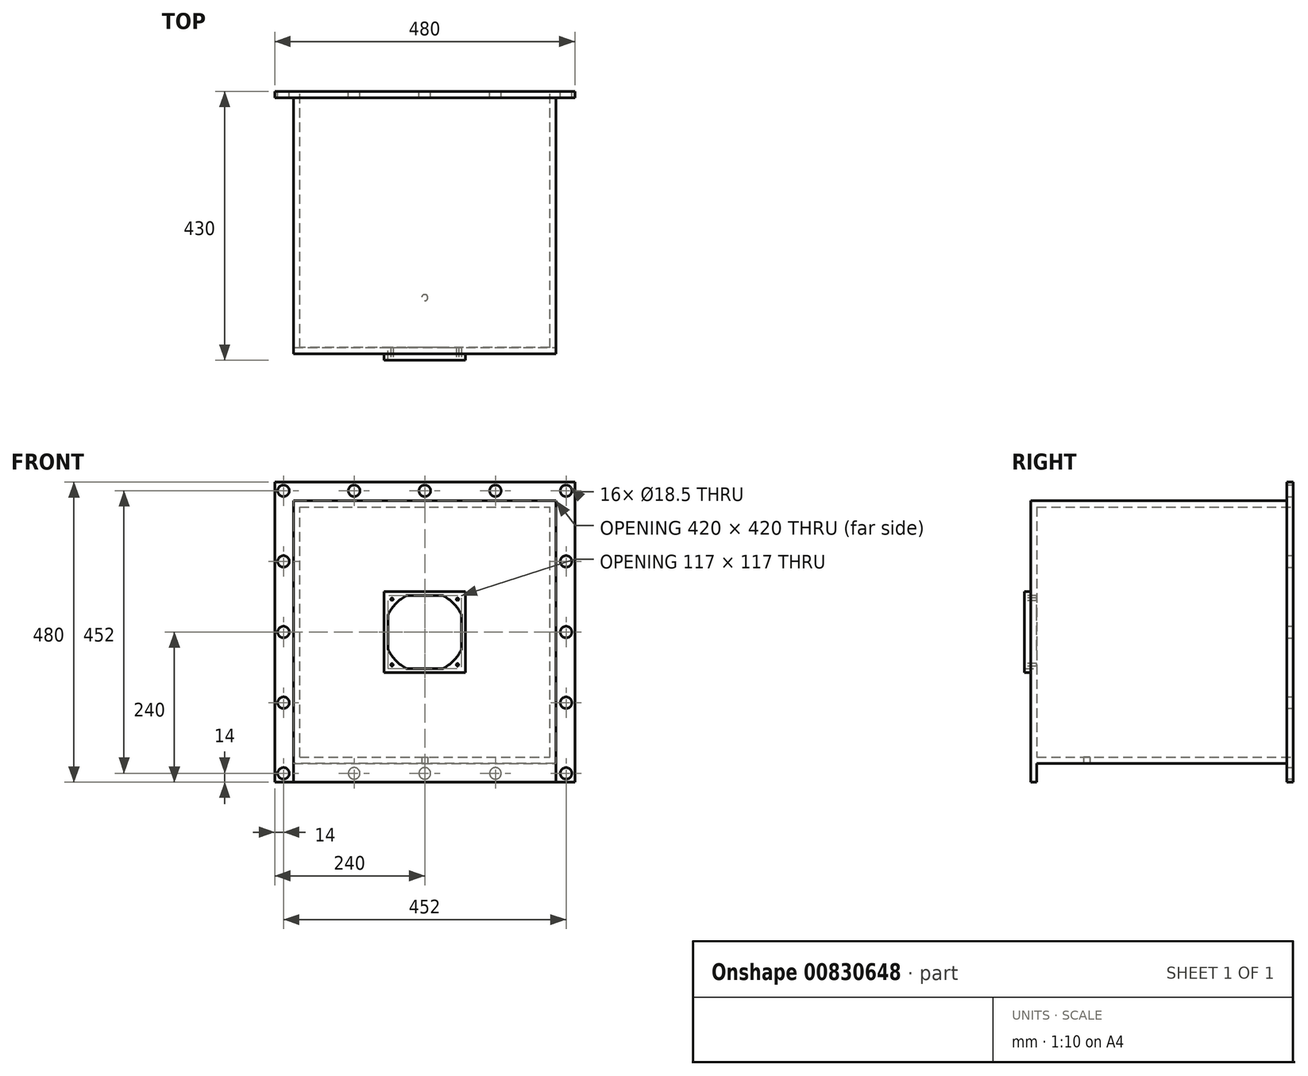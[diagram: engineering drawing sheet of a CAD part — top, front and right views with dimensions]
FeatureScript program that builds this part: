
annotation { "Feature Type Name" : "Feature", "Feature Type Description" : "" }
export const myFeature = defineFeature(function(context is Context, id is Id, definition is map)
    precondition{}
    {
        {
            var Q0;
            Q0=qCreatedBy(makeId("Front.planeOp"),FACE);
            var sketch = newSketch(context, id + "F0", { "sketchPlane" : qUnion([Q0])});
            skLineSegment(sketch, "E0", {"start": v(0, 306.37) * mm, "end": v(0, -317.21) * mm, "construction": true});
            skLineSegment(sketch, "E1", {"start": v(-443.03, 0) * mm, "end": v(583.03, 0) * mm, "construction": true});
            skLineSegment(sketch, "E2.bottom", {"start": v(-210, 210) * mm, "end": v(210, 210) * mm});
            skLineSegment(sketch, "E2.top", {"start": v(-210, -210) * mm, "end": v(210, -210) * mm});
            skLineSegment(sketch, "E2.left", {"start": v(-210, 210) * mm, "end": v(-210, -210) * mm});
            skLineSegment(sketch, "E2.right", {"start": v(210, 210) * mm, "end": v(210, -210) * mm});
            skSolve(sketch);
        }
        {
            var Q0;
            Q0 = qSketchRegion(id + "F0", true);
            extrude(context, id + "F1", {"entities" : qUnion([Q0]), "depth" : 420 * mm, "offsetDistance" : 25 * mm});
        }
        {
            var Q0;
            Q0=makeQuery(id+"F0.imprint","IMPRINT",FACE,{"disambiguationData":[TD([[makeQuery(id+"F0.imprint","IMPRINT",EDGE,{"derivedFrom":sQuery(id+"F0.wireOp",EDGE,"E2.bottom")}),-1.0]])]});
            var sketch = newSketch(context, id + "F2", { "sketchPlane" : qUnion([Q0])});
            skLineSegment(sketch, "E3.bottom", {"start": v(200, 200) * mm, "end": v(-200, 200) * mm});
            skLineSegment(sketch, "E3.top", {"start": v(200, -200) * mm, "end": v(-200, -200) * mm});
            skLineSegment(sketch, "E3.left", {"start": v(200, 200) * mm, "end": v(200, -200) * mm});
            skLineSegment(sketch, "E3.right", {"start": v(-200, 200) * mm, "end": v(-200, -200) * mm});
            skSolve(sketch);
        }
        {
            var Q0;
            Q0 = qSketchRegion(id + "F2", true);
            extrude(context, id + "F3", {"entities" : qUnion([Q0]), "operationType" : NewBodyOperationType.REMOVE, "depth" : 410 * mm, "offsetDistance" : 25 * mm});
        }
        {
            var Q0;
            Q0=makeQuery(id+"F0.imprint","IMPRINT",FACE,{"disambiguationData":[TD([[makeQuery(id+"F0.imprint","IMPRINT",EDGE,{"derivedFrom":sQuery(id+"F0.wireOp",EDGE,"E2.bottom")}),-1.0]])]});
            var sketch = newSketch(context, id + "F4", { "sketchPlane" : qUnion([Q0])});
            skLineSegment(sketch, "E4.0", {"start": v(-240, 240) * mm, "end": v(240, 240) * mm});
            skLineSegment(sketch, "E4.1", {"start": v(-240, 240) * mm, "end": v(-240, -240) * mm});
            skLineSegment(sketch, "E4.2", {"start": v(-240, -240) * mm, "end": v(240, -240) * mm});
            skLineSegment(sketch, "E4.3", {"start": v(240, 240) * mm, "end": v(240, -240) * mm});
            skLineSegment(sketch, "E5.0", {"start": v(210, 210) * mm, "end": v(210, -210) * mm});
            skLineSegment(sketch, "E6.0", {"start": v(-210, 210) * mm, "end": v(210, 210) * mm});
            skLineSegment(sketch, "E7.0", {"start": v(-210, 210) * mm, "end": v(-210, -210) * mm});
            skLineSegment(sketch, "E8.0", {"start": v(-210, -210) * mm, "end": v(210, -210) * mm});
            skSolve(sketch);
        }
        {
            var Q0;
            Q0 = qSketchRegion(id + "F4", true);
            extrude(context, id + "F5", {"entities" : qUnion([Q0]), "operationType" : NewBodyOperationType.ADD, "depth" : 10 * mm, "offsetDistance" : 25 * mm});
        }
        {
            var Q0;
            Q0=makeQuery(id+"F1.opExtrude","CAP_FACE",FACE,{"disambiguationData":[OSD([sQuery(id+"F0.wireOp",EDGE,"E2.bottom"),sQuery(id+"F0.wireOp",EDGE,"E2.top"),sQuery(id+"F0.wireOp",EDGE,"E2.left"),sQuery(id+"F0.wireOp",EDGE,"E2.right")])],"isStart":false});
            var sketch = newSketch(context, id + "F6", { "sketchPlane" : qUnion([Q0])});
            skLineSegment(sketch, "E9", {"start": v(0, 340.6) * mm, "end": v(0, -378.07) * mm, "construction": true});
            skPoint(sketch, "E9.endSnap0", {"position": v(0, -210) * mm});
            skLineSegment(sketch, "E10", {"start": v(-383.48, 0) * mm, "end": v(426.16, 0) * mm, "construction": true});
            skLineSegment(sketch, "E11.bottom", {"start": v(-65, 65) * mm, "end": v(65, 65) * mm});
            skLineSegment(sketch, "E11.top", {"start": v(-65, -65) * mm, "end": v(65, -65) * mm});
            skLineSegment(sketch, "E11.left", {"start": v(-65, 65) * mm, "end": v(-65, -65) * mm});
            skLineSegment(sketch, "E11.right", {"start": v(65, 65) * mm, "end": v(65, -65) * mm});
            skSolve(sketch);
        }
        {
            var Q0;
            Q0 = qSketchRegion(id + "F6", true);
            extrude(context, id + "F7", {"entities" : qUnion([Q0]), "operationType" : NewBodyOperationType.ADD, "depth" : 10 * mm, "offsetDistance" : 25 * mm});
        }
        {
            var Q0;
            Q0=makeQuery(id+"F7.opExtrude","CAP_FACE",FACE,{"disambiguationData":[OSD([sQuery(id+"F6.wireOp",EDGE,"E11.bottom"),sQuery(id+"F6.wireOp",EDGE,"E11.top"),sQuery(id+"F6.wireOp",EDGE,"E11.left"),sQuery(id+"F6.wireOp",EDGE,"E11.right")])],"isStart":false});
            var sketch = newSketch(context, id + "F8", { "sketchPlane" : qUnion([Q0])});
            skLineSegment(sketch, "E12", {"start": v(0, 129.06) * mm, "end": v(0, -141.19) * mm, "construction": true});
            skLineSegment(sketch, "E13", {"start": v(-149.42, 0) * mm, "end": v(152.02, 0) * mm, "construction": true});
            skArc(sketch, "E14", {"start": v(-28.33, 58.5) * mm, "mid": v(-45.96, 45.96) * mm, "end": v(-58.5, 28.33) * mm});
            skLineSegment(sketch, "E15.bottom", {"start": v(-28.33, 58.5) * mm, "end": v(28.33, 58.5) * mm});
            skLineSegment(sketch, "E15.top", {"start": v(-28.33, -58.5) * mm, "end": v(28.33, -58.5) * mm});
            skLineSegment(sketch, "E15.left", {"start": v(-58.5, 28.33) * mm, "end": v(-58.5, -28.33) * mm});
            skLineSegment(sketch, "E15.right", {"start": v(58.5, 28.33) * mm, "end": v(58.5, -28.33) * mm});
            skArc(sketch, "E16.trimOffspring", {"start": v(-58.5, -28.33) * mm, "mid": v(-45.96, -45.96) * mm, "end": v(-28.33, -58.5) * mm});
            skArc(sketch, "E17.trimOffspring", {"start": v(28.33, -58.5) * mm, "mid": v(45.96, -45.96) * mm, "end": v(58.5, -28.33) * mm});
            skArc(sketch, "E18.trimOffspring", {"start": v(58.5, 28.33) * mm, "mid": v(45.96, 45.96) * mm, "end": v(28.33, 58.5) * mm});
            skSolve(sketch);
        }
        {
            var Q0;
            Q0 = qSketchRegion(id + "F8", true);
            extrude(context, id + "F9", {"entities" : qUnion([Q0]), "operationType" : NewBodyOperationType.REMOVE, "endBound" : BoundingType.UP_TO_NEXT, "oppositeDirection" : true, "depth" : 25 * mm, "offsetDistance" : 25 * mm});
        }
        {
            var Q0;
            Q0=makeQuery(id+"F7.opExtrude","CAP_FACE",FACE,{"disambiguationData":[OSD([sQuery(id+"F6.wireOp",EDGE,"E11.bottom"),sQuery(id+"F6.wireOp",EDGE,"E11.top"),sQuery(id+"F6.wireOp",EDGE,"E11.left"),sQuery(id+"F6.wireOp",EDGE,"E11.right")])],"isStart":false});
            var sketch = newSketch(context, id + "F10", { "sketchPlane" : qUnion([Q0])});
            skLineSegment(sketch, "E19", {"start": v(0, 121.68) * mm, "end": v(0, -124.9) * mm, "construction": true});
            skLineSegment(sketch, "E20", {"start": v(-130.66, 0) * mm, "end": v(137.37, 0) * mm, "construction": true});
            skCircle(sketch, "E21", {"center": v(52.4, 52.4) * mm, "radius": 2 * mm});
            skCircle(sketch, "E22.MirrorC", {"center": v(52.4, -52.4) * mm, "radius": 2 * mm});
            skCircle(sketch, "E23.MirrorC", {"center": v(-52.4, 52.4) * mm, "radius": 2 * mm});
            skCircle(sketch, "E24.MirrorC", {"center": v(-52.4, -52.4) * mm, "radius": 2 * mm});
            skSolve(sketch);
        }
        {
            var Q0;
            Q0 = qSketchRegion(id + "F10", true);
            extrude(context, id + "F11", {"entities" : qUnion([Q0]), "operationType" : NewBodyOperationType.REMOVE, "endBound" : BoundingType.UP_TO_NEXT, "oppositeDirection" : true, "depth" : 25 * mm, "offsetDistance" : 25 * mm});
        }
        {
            var Q0;
            Q0=makeQuery(id+"F5.boolean.opBoolean","MERGE",FACE,{"derivedFrom":[makeQuery(id+"F1.opExtrude","CAP_FACE",FACE,{"disambiguationData":[OSD([sQuery(id+"F0.wireOp",EDGE,"E2.bottom"),sQuery(id+"F0.wireOp",EDGE,"E2.top"),sQuery(id+"F0.wireOp",EDGE,"E2.left"),sQuery(id+"F0.wireOp",EDGE,"E2.right")])],"isStart":true}),makeQuery(id+"F5.opExtrude","CAP_FACE",FACE,{"disambiguationData":[OSD([sQuery(id+"F4.wireOp",EDGE,"E4.0"),sQuery(id+"F4.wireOp",EDGE,"E4.1"),sQuery(id+"F4.wireOp",EDGE,"E4.2"),sQuery(id+"F4.wireOp",EDGE,"E4.3"),sQuery(id+"F4.wireOp",EDGE,"E5.0"),sQuery(id+"F4.wireOp",EDGE,"E6.0"),sQuery(id+"F4.wireOp",EDGE,"E7.0"),sQuery(id+"F4.wireOp",EDGE,"E8.0")])],"isStart":true})]});
            var sketch = newSketch(context, id + "F12", { "sketchPlane" : qUnion([Q0])});
            skLineSegment(sketch, "E25.0", {"start": v(-210, 210) * mm, "end": v(210, 210) * mm});
            skLineSegment(sketch, "E25.1", {"start": v(-210, 210) * mm, "end": v(-210, -210) * mm});
            skLineSegment(sketch, "E25.2", {"start": v(-210, -210) * mm, "end": v(210, -210) * mm});
            skLineSegment(sketch, "E25.3", {"start": v(210, 210) * mm, "end": v(210, -210) * mm});
            skSolve(sketch);
        }
        {
            var Q0;
            Q0 = qSketchRegion(id + "F12", true);
            extrude(context, id + "F13", {"entities" : qUnion([Q0]), "operationType" : NewBodyOperationType.REMOVE, "oppositeDirection" : true, "depth" : 0.5 * mm, "offsetDistance" : 25 * mm});
        }
        {
            var Q0;
            Q0=makeQuery(id+"F13.boolean.opBoolean","COPY",EDGE,{"derivedFrom":makeQuery(id+"F13.opExtrude","SWEPT_EDGE",EDGE,{"disambiguationData":[OSD([sQuery(id+"F12.wireOp",EDGE,"E25.0"),sQuery(id+"F12.wireOp",EDGE,"E25.1")])]})});
            var Q1;
            Q1=makeQuery(id+"F13.boolean.opBoolean","COPY",EDGE,{"derivedFrom":makeQuery(id+"F13.opExtrude","SWEPT_EDGE",EDGE,{"disambiguationData":[OSD([sQuery(id+"F12.wireOp",EDGE,"E25.0"),sQuery(id+"F12.wireOp",EDGE,"E25.3")])]})});
            var Q2;
            Q2=makeQuery(id+"F13.boolean.opBoolean","COPY",EDGE,{"derivedFrom":makeQuery(id+"F13.opExtrude","SWEPT_EDGE",EDGE,{"disambiguationData":[OSD([sQuery(id+"F12.wireOp",EDGE,"E25.2"),sQuery(id+"F12.wireOp",EDGE,"E25.3")])]})});
            var Q3;
            Q3=makeQuery(id+"F13.boolean.opBoolean","COPY",EDGE,{"derivedFrom":makeQuery(id+"F13.opExtrude","SWEPT_EDGE",EDGE,{"disambiguationData":[OSD([sQuery(id+"F12.wireOp",EDGE,"E25.1"),sQuery(id+"F12.wireOp",EDGE,"E25.2")])]})});
            fillet(context, id + "F14", {"entities" : qUnion([Q0, Q1, Q2, Q3]), "radius" : 2 * mm, "tangentPropagation" : true, "allowEdgeOverflow" : false});
        }
        {
            var Q0;
            Q0=makeQuery(id+"F5.boolean.opBoolean","MERGE",FACE,{"derivedFrom":[makeQuery(id+"F1.opExtrude","CAP_FACE",FACE,{"disambiguationData":[OSD([sQuery(id+"F0.wireOp",EDGE,"E2.bottom"),sQuery(id+"F0.wireOp",EDGE,"E2.top"),sQuery(id+"F0.wireOp",EDGE,"E2.left"),sQuery(id+"F0.wireOp",EDGE,"E2.right")])],"isStart":true}),makeQuery(id+"F5.opExtrude","CAP_FACE",FACE,{"disambiguationData":[OSD([sQuery(id+"F4.wireOp",EDGE,"E4.0"),sQuery(id+"F4.wireOp",EDGE,"E4.1"),sQuery(id+"F4.wireOp",EDGE,"E4.2"),sQuery(id+"F4.wireOp",EDGE,"E4.3"),sQuery(id+"F4.wireOp",EDGE,"E5.0"),sQuery(id+"F4.wireOp",EDGE,"E6.0"),sQuery(id+"F4.wireOp",EDGE,"E7.0"),sQuery(id+"F4.wireOp",EDGE,"E8.0")])],"isStart":true})]});
            var sketch = newSketch(context, id + "F15", { "sketchPlane" : qUnion([Q0])});
            skLineSegment(sketch, "E26.0", {"start": v(226, 226) * mm, "end": v(-226, 226) * mm, "construction": true});
            skLineSegment(sketch, "E26.1", {"start": v(226, 226) * mm, "end": v(226, -226) * mm, "construction": true});
            skLineSegment(sketch, "E26.2", {"start": v(226, -226) * mm, "end": v(-226, -226) * mm, "construction": true});
            skLineSegment(sketch, "E26.3", {"start": v(-226, 226) * mm, "end": v(-226, -226) * mm, "construction": true});
            skCircle(sketch, "E27", {"center": v(-226, 226) * mm, "radius": 9.25 * mm});
            skCircle(sketch, "E28", {"center": v(226, 226) * mm, "radius": 9.25 * mm});
            skCircle(sketch, "E29", {"center": v(-226, -226) * mm, "radius": 9.25 * mm});
            skCircle(sketch, "E30", {"center": v(226, -226) * mm, "radius": 9.25 * mm});
            skCircle(sketch, "E31.1.0.0", {"center": v(-113, 226) * mm, "radius": 9.25 * mm});
            skCircle(sketch, "E31.2.0.0", {"center": v(0, 226) * mm, "radius": 9.25 * mm});
            skCircle(sketch, "E31.3.0.0", {"center": v(113, 226) * mm, "radius": 9.25 * mm});
            skLineSegment(sketch, "E31.direction1", {"start": v(-226, 226) * mm, "end": v(-113, 226) * mm, "construction": true});
            skLineSegment(sketch, "E32", {"start": v(0, 329.24) * mm, "end": v(0, -280.21) * mm, "construction": true});
            skLineSegment(sketch, "E33", {"start": v(-290.82, 0) * mm, "end": v(280.62, 0) * mm, "construction": true});
            skCircle(sketch, "E34.0.1.0", {"center": v(-226, -113) * mm, "radius": 9.25 * mm});
            skCircle(sketch, "E34.0.2.0", {"center": v(-226, 0) * mm, "radius": 9.25 * mm});
            skCircle(sketch, "E34.0.3.0", {"center": v(-226, 113) * mm, "radius": 9.25 * mm});
            skLineSegment(sketch, "E34.direction1", {"start": v(-226, -226) * mm, "end": v(-201, -226) * mm, "construction": true});
            skLineSegment(sketch, "E34.direction2", {"start": v(-226, -226) * mm, "end": v(-226, -113) * mm, "construction": true});
            skCircle(sketch, "E35.MirrorC", {"center": v(226, 113) * mm, "radius": 9.25 * mm});
            skCircle(sketch, "E36.MirrorC", {"center": v(226, 0) * mm, "radius": 9.25 * mm});
            skCircle(sketch, "E37.MirrorC", {"center": v(226, -113) * mm, "radius": 9.25 * mm});
            skCircle(sketch, "E38.MirrorC", {"center": v(-113, -226) * mm, "radius": 9.25 * mm});
            skCircle(sketch, "E39.MirrorC", {"center": v(0, -226) * mm, "radius": 9.25 * mm});
            skCircle(sketch, "E40.MirrorC", {"center": v(113, -226) * mm, "radius": 9.25 * mm});
            skSolve(sketch);
        }
        {
            var Q0;
            Q0 = qSketchRegion(id + "F15", true);
            extrude(context, id + "F16", {"entities" : qUnion([Q0]), "operationType" : NewBodyOperationType.REMOVE, "endBound" : BoundingType.UP_TO_NEXT, "oppositeDirection" : true, "depth" : 25 * mm, "offsetDistance" : 25 * mm});
        }
        {
            var Q0;
            Q0=makeQuery(id+"F1.opExtrude","SWEPT_FACE",FACE,{"disambiguationData":[OSD([sQuery(id+"F0.wireOp",EDGE,"E2.top")])]});
            var sketch = newSketch(context, id + "F17", { "sketchPlane" : qUnion([Q0])});
            skLineSegment(sketch, "E41", {"start": v(0, 454.93) * mm, "end": v(0, -64.56) * mm, "construction": true});
            skLineSegment(sketch, "E42", {"start": v(-358.26, 330) * mm, "end": v(362.32, 330) * mm, "construction": true});
            skLineSegment(sketch, "E43.0", {"start": v(-210, 420) * mm, "end": v(210, 420) * mm, "construction": true});
            skCircle(sketch, "E44", {"center": v(0, 330) * mm, "radius": 5 * mm});
            skSolve(sketch);
        }
        {
            var Q0;
            Q0 = qSketchRegion(id + "F17", true);
            extrude(context, id + "F18", {"entities" : qUnion([Q0]), "operationType" : NewBodyOperationType.REMOVE, "endBound" : BoundingType.UP_TO_NEXT, "oppositeDirection" : true, "depth" : 25 * mm, "offsetDistance" : 25 * mm});
        }
        {
            var Q0;
            Q0=makeQuery(id+"F1.opExtrude","SWEPT_FACE",FACE,{"disambiguationData":[OSD([sQuery(id+"F0.wireOp",EDGE,"E2.top")])]});
            var sketch = newSketch(context, id + "F19", { "sketchPlane" : qUnion([Q0])});
            skLineSegment(sketch, "E45.0", {"start": v(-210, 420) * mm, "end": v(210, 420) * mm});
            skLineSegment(sketch, "E46", {"start": v(-210, 410) * mm, "end": v(210, 410) * mm});
            skLineSegment(sketch, "E47", {"start": v(-210, 420) * mm, "end": v(-210, 410) * mm});
            skLineSegment(sketch, "E48", {"start": v(210, 420) * mm, "end": v(210, 410) * mm});
            skSolve(sketch);
        }
        {
            var Q0;
            Q0 = qSketchRegion(id + "F19", true);
            extrude(context, id + "F20", {"entities" : qUnion([Q0]), "operationType" : NewBodyOperationType.ADD, "depth" : 30 * mm, "offsetDistance" : 25 * mm});
        }
        {
            var Q0;
            Q0=makeQuery(id+"F9.boolean.opBoolean","COPY",EDGE,{"derivedFrom":makeQuery(id+"F9.opExtrude","SWEPT_EDGE",EDGE,{"disambiguationData":[OSD([sQuery(id+"F8.wireOp",EDGE,"E14"),sQuery(id+"F8.wireOp",EDGE,"E15.left")])]})});
            var Q1;
            Q1=makeQuery(id+"F9.boolean.opBoolean","COPY",EDGE,{"derivedFrom":makeQuery(id+"F9.opExtrude","SWEPT_EDGE",EDGE,{"disambiguationData":[OSD([sQuery(id+"F8.wireOp",EDGE,"E14"),sQuery(id+"F8.wireOp",EDGE,"E15.bottom")])]})});
            var Q2;
            Q2=makeQuery(id+"F9.boolean.opBoolean","COPY",EDGE,{"derivedFrom":makeQuery(id+"F9.opExtrude","SWEPT_EDGE",EDGE,{"disambiguationData":[OSD([sQuery(id+"F8.wireOp",EDGE,"E15.left"),sQuery(id+"F8.wireOp",EDGE,"E16.trimOffspring")])]})});
            var Q3;
            Q3=makeQuery(id+"F9.boolean.opBoolean","COPY",EDGE,{"derivedFrom":makeQuery(id+"F9.opExtrude","SWEPT_EDGE",EDGE,{"disambiguationData":[OSD([sQuery(id+"F8.wireOp",EDGE,"E15.top"),sQuery(id+"F8.wireOp",EDGE,"E16.trimOffspring")])]})});
            var Q4;
            Q4=makeQuery(id+"F9.boolean.opBoolean","COPY",EDGE,{"derivedFrom":makeQuery(id+"F9.opExtrude","SWEPT_EDGE",EDGE,{"disambiguationData":[OSD([sQuery(id+"F8.wireOp",EDGE,"E15.top"),sQuery(id+"F8.wireOp",EDGE,"E17.trimOffspring")])]})});
            var Q5;
            Q5=makeQuery(id+"F9.boolean.opBoolean","COPY",EDGE,{"derivedFrom":makeQuery(id+"F9.opExtrude","SWEPT_EDGE",EDGE,{"disambiguationData":[OSD([sQuery(id+"F8.wireOp",EDGE,"E15.right"),sQuery(id+"F8.wireOp",EDGE,"E17.trimOffspring")])]})});
            var Q6;
            Q6=makeQuery(id+"F9.boolean.opBoolean","COPY",EDGE,{"derivedFrom":makeQuery(id+"F9.opExtrude","SWEPT_EDGE",EDGE,{"disambiguationData":[OSD([sQuery(id+"F8.wireOp",EDGE,"E15.right"),sQuery(id+"F8.wireOp",EDGE,"E18.trimOffspring")])]})});
            var Q7;
            Q7=makeQuery(id+"F9.boolean.opBoolean","COPY",EDGE,{"derivedFrom":makeQuery(id+"F9.opExtrude","SWEPT_EDGE",EDGE,{"disambiguationData":[OSD([sQuery(id+"F8.wireOp",EDGE,"E15.bottom"),sQuery(id+"F8.wireOp",EDGE,"E18.trimOffspring")])]})});
            fillet(context, id + "F21", {"entities" : qUnion([Q0, Q1, Q2, Q3, Q4, Q5, Q6, Q7]), "radius" : 3 * mm, "tangentPropagation" : true, "allowEdgeOverflow" : false});
        }
    });
